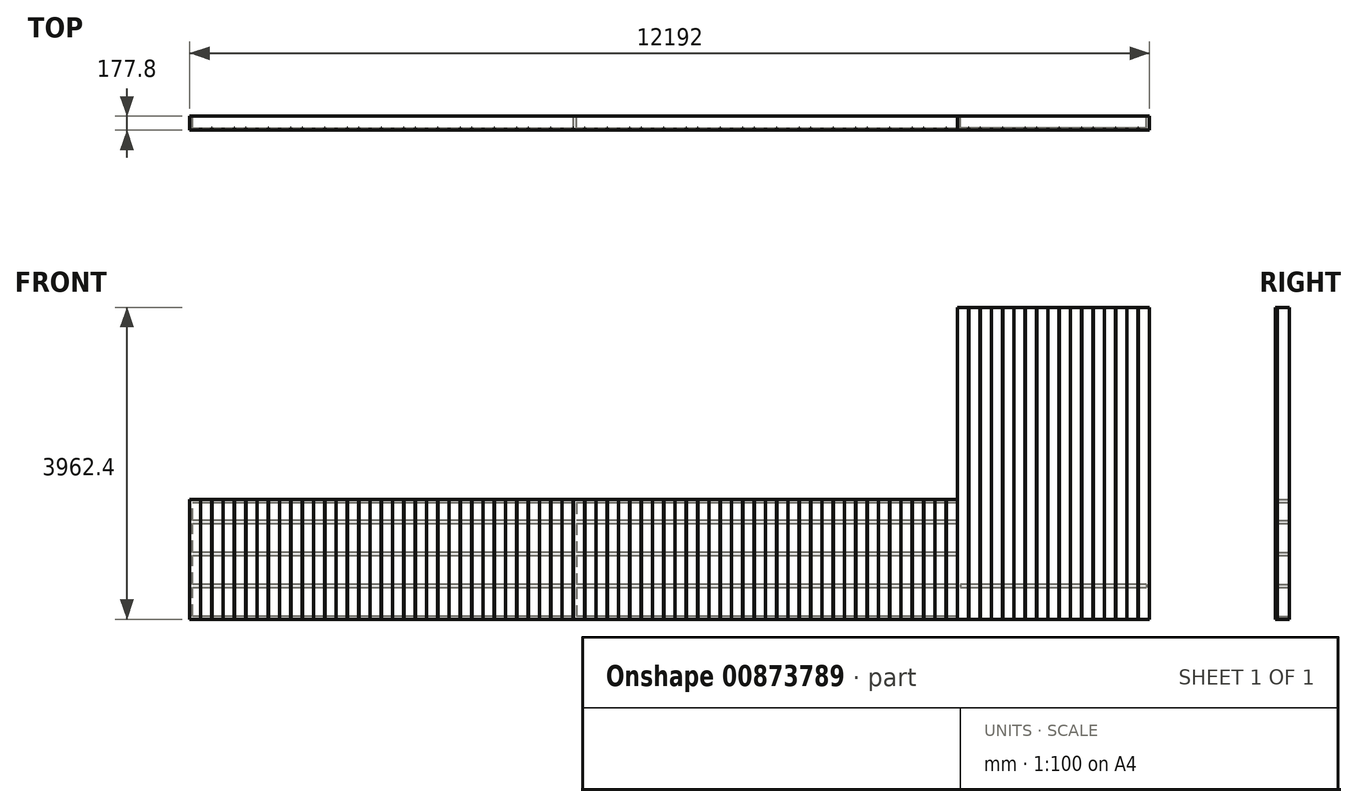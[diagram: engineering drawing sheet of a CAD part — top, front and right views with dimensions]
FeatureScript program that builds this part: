
annotation { "Feature Type Name" : "Feature", "Feature Type Description" : "" }
export const myFeature = defineFeature(function(context is Context, id is Id, definition is map)
    precondition{}
    {
        {
            var Q0;
            Q0=qCreatedBy(makeId("Front.planeOp"),FACE);
            var sketch = newSketch(context, id + "F0", { "sketchPlane" : qUnion([Q0])});
            skLineSegment(sketch, "E0", {"start": v(0, 0) * mm, "end": v(0, 1524) * mm});
            skLineSegment(sketch, "E1", {"start": v(0, 1524) * mm, "end": v(9753.6, 1524) * mm});
            skLineSegment(sketch, "E2", {"start": v(9753.6, 1524) * mm, "end": v(9753.6, 3962.4) * mm});
            skLineSegment(sketch, "E3", {"start": v(9753.6, 3962.4) * mm, "end": v(12192, 3962.4) * mm});
            skLineSegment(sketch, "E4", {"start": v(12192, 3962.4) * mm, "end": v(12192, 0) * mm});
            skLineSegment(sketch, "E5", {"start": v(12192, 0) * mm, "end": v(0, 0) * mm});
            skLineSegment(sketch, "E6.0", {"start": v(38.1, 38.1) * mm, "end": v(38.1, 1485.9) * mm});
            skLineSegment(sketch, "E6.1", {"start": v(9791.7, 1485.9) * mm, "end": v(9791.7, 3924.3) * mm});
            skLineSegment(sketch, "E6.2", {"start": v(9791.7, 3924.3) * mm, "end": v(12153.9, 3924.3) * mm});
            skLineSegment(sketch, "E6.3", {"start": v(38.1, 1485.9) * mm, "end": v(9791.7, 1485.9) * mm});
            skLineSegment(sketch, "E6.4", {"start": v(12153.9, 3924.3) * mm, "end": v(12153.9, 38.1) * mm});
            skLineSegment(sketch, "E6.5", {"start": v(12153.9, 38.1) * mm, "end": v(38.1, 38.1) * mm});
            skLineSegment(sketch, "E7", {"start": v(9791.7, 1485.9) * mm, "end": v(12153.9, 1485.9) * mm});
            skLineSegment(sketch, "E8", {"start": v(12153.9, 1524) * mm, "end": v(9791.7, 1524) * mm});
            skLineSegment(sketch, "E9", {"start": v(9791.7, 1485.9) * mm, "end": v(9791.7, 38.1) * mm});
            skLineSegment(sketch, "E10", {"start": v(9753.6, 1485.9) * mm, "end": v(9753.6, 38.1) * mm});
            skLineSegment(sketch, "E11", {"start": v(19.05, 0) * mm, "end": v(19.05, 1524) * mm, "construction": true});
            skLineSegment(sketch, "E12", {"start": v(4895.85, 1524) * mm, "end": v(4895.85, 0) * mm, "construction": true});
            skLineSegment(sketch, "E13.0", {"start": v(4876.8, 1524) * mm, "end": v(4876.8, 0) * mm});
            skLineSegment(sketch, "E14.0", {"start": v(4914.9, 1524) * mm, "end": v(4914.9, 0) * mm});
            skLineSegment(sketch, "E15", {"start": v(0, 19.05) * mm, "end": v(12192, 19.05) * mm, "construction": true});
            skLineSegment(sketch, "E16", {"start": v(38.1, 425.45) * mm, "end": v(4876.8, 425.45) * mm, "construction": true});
            skLineSegment(sketch, "E17.0.1.0", {"start": v(38.1, 831.85) * mm, "end": v(4876.8, 831.85) * mm, "construction": true});
            skLineSegment(sketch, "E17.0.2.0", {"start": v(38.1, 1238.25) * mm, "end": v(4876.8, 1238.25) * mm, "construction": true});
            skLineSegment(sketch, "E17.direction1", {"start": v(38.1, 425.45) * mm, "end": v(38.1, 425.45) * mm});
            skLineSegment(sketch, "E17.direction2", {"start": v(38.1, 425.45) * mm, "end": v(38.1, 831.85) * mm, "construction": true});
            skLineSegment(sketch, "E18", {"start": v(4914.9, 1238.25) * mm, "end": v(9753.6, 1238.25) * mm, "construction": true});
            skLineSegment(sketch, "E19", {"start": v(4914.9, 831.85) * mm, "end": v(9753.6, 831.85) * mm, "construction": true});
            skLineSegment(sketch, "E20", {"start": v(4914.9, 425.45) * mm, "end": v(9753.6, 425.45) * mm, "construction": true});
            skLineSegment(sketch, "E21", {"start": v(9791.7, 1238.25) * mm, "end": v(12153.9, 1238.25) * mm, "construction": true});
            skLineSegment(sketch, "E22", {"start": v(9791.7, 831.85) * mm, "end": v(12153.9, 831.85) * mm, "construction": true});
            skLineSegment(sketch, "E23", {"start": v(9791.7, 425.45) * mm, "end": v(12153.9, 425.45) * mm, "construction": true});
            skLineSegment(sketch, "E24", {"start": v(12153.9, 425.45) * mm, "end": v(12153.9, 1485.9) * mm});
            skLineSegment(sketch, "E25", {"start": v(12153.9, 1504.95) * mm, "end": v(9791.7, 1504.95) * mm, "construction": true});
            skLineSegment(sketch, "E26", {"start": v(9791.7, 1911.35) * mm, "end": v(12153.9, 1911.35) * mm, "construction": true});
            skLineSegment(sketch, "E27.0.1.0", {"start": v(9791.7, 2317.75) * mm, "end": v(12153.9, 2317.75) * mm, "construction": true});
            skLineSegment(sketch, "E27.0.2.0", {"start": v(9791.7, 2724.15) * mm, "end": v(12153.9, 2724.15) * mm, "construction": true});
            skLineSegment(sketch, "E27.0.3.0", {"start": v(9791.7, 3130.55) * mm, "end": v(12153.9, 3130.55) * mm, "construction": true});
            skLineSegment(sketch, "E27.0.4.0", {"start": v(9791.7, 3536.95) * mm, "end": v(12153.9, 3536.95) * mm, "construction": true});
            skLineSegment(sketch, "E27.direction1", {"start": v(9791.7, 1911.35) * mm, "end": v(9791.7, 1911.35) * mm});
            skLineSegment(sketch, "E27.direction2", {"start": v(9791.7, 1911.35) * mm, "end": v(9791.7, 2317.75) * mm, "construction": true});
            skLineSegment(sketch, "E28", {"start": v(38.1, 406.4) * mm, "end": v(12153.9, 406.4) * mm});
            skLineSegment(sketch, "E29", {"start": v(12153.9, 444.5) * mm, "end": v(38.1, 444.5) * mm});
            skLineSegment(sketch, "E30", {"start": v(38.1, 812.8) * mm, "end": v(12153.9, 812.8) * mm});
            skLineSegment(sketch, "E31", {"start": v(12153.9, 850.9) * mm, "end": v(38.1, 850.9) * mm});
            skLineSegment(sketch, "E32", {"start": v(38.1, 850.9) * mm, "end": v(70.73, 865.43) * mm});
            skLineSegment(sketch, "E33", {"start": v(38.1, 1219.2) * mm, "end": v(12153.9, 1219.2) * mm});
            skLineSegment(sketch, "E34", {"start": v(12153.9, 1257.3) * mm, "end": v(38.1, 1257.3) * mm});
            skLineSegment(sketch, "E35", {"start": v(9791.7, 1892.3) * mm, "end": v(12153.9, 1892.3) * mm});
            skLineSegment(sketch, "E36", {"start": v(9791.7, 1930.4) * mm, "end": v(12153.9, 1930.4) * mm});
            skLineSegment(sketch, "E37", {"start": v(12153.9, 2298.7) * mm, "end": v(9791.7, 2298.7) * mm});
            skLineSegment(sketch, "E38", {"start": v(9791.7, 2336.8) * mm, "end": v(12153.9, 2336.8) * mm});
            skLineSegment(sketch, "E39", {"start": v(12153.9, 2336.8) * mm, "end": v(12144.47, 2361.14) * mm});
            skLineSegment(sketch, "E40", {"start": v(12153.9, 2705.1) * mm, "end": v(9791.7, 2705.1) * mm});
            skLineSegment(sketch, "E41", {"start": v(9791.7, 2743.2) * mm, "end": v(12153.9, 2743.2) * mm});
            skLineSegment(sketch, "E42", {"start": v(12153.9, 3111.5) * mm, "end": v(9791.7, 3111.5) * mm});
            skLineSegment(sketch, "E43", {"start": v(9791.7, 3149.6) * mm, "end": v(12153.9, 3149.6) * mm});
            skLineSegment(sketch, "E44", {"start": v(12153.9, 3517.9) * mm, "end": v(9791.7, 3517.9) * mm});
            skLineSegment(sketch, "E45", {"start": v(9791.7, 3556) * mm, "end": v(12153.9, 3556) * mm});
            skSolve(sketch);
        }
        {
            var Q0;
            Q0 = qSketchRegion(id + "F0", true);
            var Q1;
            {var subQ0=sQuery(id+"F0.wireOp",EDGE,"E33");var subQ1=sQuery(id+"F0.wireOp",EDGE,"E6.0");var subQ2=makeQuery(id+"F0.imprint","INTERSECT",VERTEX,{"derivedFrom":[subQ1,subQ0]});Q1=makeQuery(id+"F0.imprint","IMPRINT",FACE,{"disambiguationData":[TD([[makeQuery(id+"F0.imprint","IMPRINT",EDGE,{"disambiguationData":[TD([[subQ2,-1.0]])],"derivedFrom":subQ1}),-1.0]])]});}
            var Q2;
            {var subQ0=sQuery(id+"F0.wireOp",EDGE,"E34");var subQ1=sQuery(id+"F0.wireOp",EDGE,"E10");var subQ2=makeQuery(id+"F0.imprint","INTERSECT",VERTEX,{"derivedFrom":[subQ1,subQ0]});Q2=makeQuery(id+"F0.imprint","IMPRINT",FACE,{"disambiguationData":[TD([[makeQuery(id+"F0.imprint","IMPRINT",EDGE,{"disambiguationData":[TD([[subQ2,-1.0]])],"derivedFrom":subQ1}),-1.0]])]});}
            var Q3;
            {var subQ0=sQuery(id+"F0.wireOp",EDGE,"E13.0");var subQ1=sQuery(id+"F0.wireOp",EDGE,"E6.3");var subQ2=makeQuery(id+"F0.imprint","INTERSECT",VERTEX,{"derivedFrom":[subQ1,subQ0]});Q3=makeQuery(id+"F0.imprint","IMPRINT",FACE,{"disambiguationData":[TD([[makeQuery(id+"F0.imprint","IMPRINT",EDGE,{"disambiguationData":[TD([[subQ2,-1.0]])],"derivedFrom":subQ1}),-1.0]])]});}
            var Q4;
            {var subQ0=sQuery(id+"F0.wireOp",EDGE,"E33");var subQ1=sQuery(id+"F0.wireOp",EDGE,"E13.0");var subQ2=makeQuery(id+"F0.imprint","INTERSECT",VERTEX,{"derivedFrom":[subQ1,subQ0]});Q4=makeQuery(id+"F0.imprint","IMPRINT",FACE,{"disambiguationData":[TD([[makeQuery(id+"F0.imprint","IMPRINT",EDGE,{"disambiguationData":[TD([[subQ2,-1.0]])],"derivedFrom":subQ1}),1.0]])]});}
            var Q5;
            {var subQ0=sQuery(id+"F0.wireOp",EDGE,"E34");var subQ1=sQuery(id+"F0.wireOp",EDGE,"E13.0");var subQ2=makeQuery(id+"F0.imprint","INTERSECT",VERTEX,{"derivedFrom":[subQ1,subQ0]});Q5=makeQuery(id+"F0.imprint","IMPRINT",FACE,{"disambiguationData":[TD([[makeQuery(id+"F0.imprint","IMPRINT",EDGE,{"disambiguationData":[TD([[subQ2,-1.0]])],"derivedFrom":subQ1}),1.0]])]});}
            var Q6;
            {var subQ0=sQuery(id+"F0.wireOp",EDGE,"E31");var subQ1=sQuery(id+"F0.wireOp",EDGE,"E13.0");var subQ2=makeQuery(id+"F0.imprint","INTERSECT",VERTEX,{"derivedFrom":[subQ1,subQ0]});Q6=makeQuery(id+"F0.imprint","IMPRINT",FACE,{"disambiguationData":[TD([[makeQuery(id+"F0.imprint","IMPRINT",EDGE,{"disambiguationData":[TD([[subQ2,-1.0]])],"derivedFrom":subQ1}),1.0]])]});}
            var Q7;
            {var subQ0=sQuery(id+"F0.wireOp",EDGE,"E31");var subQ1=sQuery(id+"F0.wireOp",EDGE,"E10");var subQ2=makeQuery(id+"F0.imprint","INTERSECT",VERTEX,{"derivedFrom":[subQ1,subQ0]});Q7=makeQuery(id+"F0.imprint","IMPRINT",FACE,{"disambiguationData":[TD([[makeQuery(id+"F0.imprint","IMPRINT",EDGE,{"disambiguationData":[TD([[subQ2,-1.0]])],"derivedFrom":subQ1}),-1.0]])]});}
            var Q8;
            {var subQ0=sQuery(id+"F0.wireOp",EDGE,"E30");var subQ1=sQuery(id+"F0.wireOp",EDGE,"E6.0");var subQ2=makeQuery(id+"F0.imprint","INTERSECT",VERTEX,{"derivedFrom":[subQ1,subQ0]});Q8=makeQuery(id+"F0.imprint","IMPRINT",FACE,{"disambiguationData":[TD([[makeQuery(id+"F0.imprint","IMPRINT",EDGE,{"disambiguationData":[TD([[subQ2,-1.0]])],"derivedFrom":subQ1}),-1.0]])]});}
            var Q9;
            {var subQ0=sQuery(id+"F0.wireOp",EDGE,"E30");var subQ1=sQuery(id+"F0.wireOp",EDGE,"E13.0");var subQ2=makeQuery(id+"F0.imprint","INTERSECT",VERTEX,{"derivedFrom":[subQ1,subQ0]});Q9=makeQuery(id+"F0.imprint","IMPRINT",FACE,{"disambiguationData":[TD([[makeQuery(id+"F0.imprint","IMPRINT",EDGE,{"disambiguationData":[TD([[subQ2,-1.0]])],"derivedFrom":subQ1}),1.0]])]});}
            var Q10;
            {var subQ0=sQuery(id+"F0.wireOp",EDGE,"E14.0");var subQ1=sQuery(id+"F0.wireOp",EDGE,"E6.5");var subQ2=makeQuery(id+"F0.imprint","INTERSECT",VERTEX,{"derivedFrom":[subQ1,subQ0]});Q10=makeQuery(id+"F0.imprint","IMPRINT",FACE,{"disambiguationData":[TD([[makeQuery(id+"F0.imprint","IMPRINT",EDGE,{"disambiguationData":[TD([[subQ2,-1.0]])],"derivedFrom":subQ1}),-1.0]])]});}
            var Q11;
            {var subQ0=sQuery(id+"F0.wireOp",EDGE,"E29");var subQ1=sQuery(id+"F0.wireOp",EDGE,"E13.0");var subQ2=makeQuery(id+"F0.imprint","INTERSECT",VERTEX,{"derivedFrom":[subQ1,subQ0]});Q11=makeQuery(id+"F0.imprint","IMPRINT",FACE,{"disambiguationData":[TD([[makeQuery(id+"F0.imprint","IMPRINT",EDGE,{"disambiguationData":[TD([[subQ2,-1.0]])],"derivedFrom":subQ1}),1.0]])]});}
            var Q12;
            {var subQ0=sQuery(id+"F0.wireOp",EDGE,"E28");var subQ1=sQuery(id+"F0.wireOp",EDGE,"E6.0");var subQ2=makeQuery(id+"F0.imprint","INTERSECT",VERTEX,{"derivedFrom":[subQ1,subQ0]});Q12=makeQuery(id+"F0.imprint","IMPRINT",FACE,{"disambiguationData":[TD([[makeQuery(id+"F0.imprint","IMPRINT",EDGE,{"disambiguationData":[TD([[subQ2,-1.0]])],"derivedFrom":subQ1}),-1.0]])]});}
            var Q13;
            {var subQ0=sQuery(id+"F0.wireOp",EDGE,"E29");var subQ1=sQuery(id+"F0.wireOp",EDGE,"E10");var subQ2=makeQuery(id+"F0.imprint","INTERSECT",VERTEX,{"derivedFrom":[subQ1,subQ0]});Q13=makeQuery(id+"F0.imprint","IMPRINT",FACE,{"disambiguationData":[TD([[makeQuery(id+"F0.imprint","IMPRINT",EDGE,{"disambiguationData":[TD([[subQ2,-1.0]])],"derivedFrom":subQ1}),-1.0]])]});}
            var Q14;
            {var subQ1=sQuery(id+"F0.wireOp",EDGE,"E6.3");var subQ3=sQuery(id+"F0.wireOp",EDGE,"E10");var subQ4=makeQuery(id+"F0.imprint","INTERSECT",VERTEX,{"derivedFrom":[subQ1,subQ3]});Q14=makeQuery(id+"F0.imprint","IMPRINT",FACE,{"disambiguationData":[TD([[makeQuery(id+"F0.imprint","IMPRINT",EDGE,{"disambiguationData":[TD([[subQ4,-1.0]])],"derivedFrom":subQ3}),1.0]])]});}
            var Q15;
            {var subQ0=sQuery(id+"F0.wireOp",EDGE,"E34");var subQ1=sQuery(id+"F0.wireOp",EDGE,"E9");var subQ2=makeQuery(id+"F0.imprint","INTERSECT",VERTEX,{"derivedFrom":[subQ1,subQ0]});Q15=makeQuery(id+"F0.imprint","IMPRINT",FACE,{"disambiguationData":[TD([[makeQuery(id+"F0.imprint","IMPRINT",EDGE,{"disambiguationData":[TD([[subQ2,-1.0]])],"derivedFrom":subQ1}),-1.0]])]});}
            var Q16;
            {var subQ0=sQuery(id+"F0.wireOp",EDGE,"E33");var subQ1=sQuery(id+"F0.wireOp",EDGE,"E9");var subQ2=makeQuery(id+"F0.imprint","INTERSECT",VERTEX,{"derivedFrom":[subQ1,subQ0]});Q16=makeQuery(id+"F0.imprint","IMPRINT",FACE,{"disambiguationData":[TD([[makeQuery(id+"F0.imprint","IMPRINT",EDGE,{"disambiguationData":[TD([[subQ2,-1.0]])],"derivedFrom":subQ1}),-1.0]])]});}
            var Q17;
            {var subQ0=sQuery(id+"F0.wireOp",EDGE,"E31");var subQ1=sQuery(id+"F0.wireOp",EDGE,"E9");var subQ2=makeQuery(id+"F0.imprint","INTERSECT",VERTEX,{"derivedFrom":[subQ1,subQ0]});Q17=makeQuery(id+"F0.imprint","IMPRINT",FACE,{"disambiguationData":[TD([[makeQuery(id+"F0.imprint","IMPRINT",EDGE,{"disambiguationData":[TD([[subQ2,-1.0]])],"derivedFrom":subQ1}),-1.0]])]});}
            var Q18;
            {var subQ0=sQuery(id+"F0.wireOp",EDGE,"E30");var subQ1=sQuery(id+"F0.wireOp",EDGE,"E9");var subQ2=makeQuery(id+"F0.imprint","INTERSECT",VERTEX,{"derivedFrom":[subQ1,subQ0]});Q18=makeQuery(id+"F0.imprint","IMPRINT",FACE,{"disambiguationData":[TD([[makeQuery(id+"F0.imprint","IMPRINT",EDGE,{"disambiguationData":[TD([[subQ2,-1.0]])],"derivedFrom":subQ1}),-1.0]])]});}
            var Q19;
            {var subQ0=sQuery(id+"F0.wireOp",EDGE,"E29");var subQ1=sQuery(id+"F0.wireOp",EDGE,"E9");var subQ2=makeQuery(id+"F0.imprint","INTERSECT",VERTEX,{"derivedFrom":[subQ1,subQ0]});Q19=makeQuery(id+"F0.imprint","IMPRINT",FACE,{"disambiguationData":[TD([[makeQuery(id+"F0.imprint","IMPRINT",EDGE,{"disambiguationData":[TD([[subQ2,-1.0]])],"derivedFrom":subQ1}),-1.0]])]});}
            var Q20;
            {var subQ0=sQuery(id+"F0.wireOp",EDGE,"E9");var subQ1=sQuery(id+"F0.wireOp",EDGE,"E6.5");var subQ2=makeQuery(id+"F0.imprint","INTERSECT",VERTEX,{"derivedFrom":[subQ1,subQ0]});Q20=makeQuery(id+"F0.imprint","IMPRINT",FACE,{"disambiguationData":[TD([[makeQuery(id+"F0.imprint","IMPRINT",EDGE,{"disambiguationData":[TD([[subQ2,-1.0]])],"derivedFrom":subQ1}),-1.0]])]});}
            var Q21;
            {var subQ1=sQuery(id+"F0.wireOp",EDGE,"E6.4");var subQ5=sQuery(id+"F0.wireOp",EDGE,"E24");var subQ6=makeQuery(id+"F0.imprint","INTERSECT",VERTEX,{"derivedFrom":[subQ1,subQ5]});Q21=makeQuery(id+"F0.imprint","IMPRINT",FACE,{"disambiguationData":[TD([[makeQuery(id+"F0.imprint","IMPRINT",EDGE,{"disambiguationData":[TD([[subQ6,-1.0]])],"derivedFrom":subQ1}),-1.0]])]});}
            var Q22;
            {var subQ0=sQuery(id+"F0.wireOp",EDGE,"E31");var subQ1=sQuery(id+"F0.wireOp",EDGE,"E9");var subQ2=makeQuery(id+"F0.imprint","INTERSECT",VERTEX,{"derivedFrom":[subQ1,subQ0]});Q22=makeQuery(id+"F0.imprint","IMPRINT",FACE,{"disambiguationData":[TD([[makeQuery(id+"F0.imprint","IMPRINT",EDGE,{"disambiguationData":[TD([[subQ2,-1.0]])],"derivedFrom":subQ1}),1.0]])]});}
            var Q23;
            {var subQ0=sQuery(id+"F0.wireOp",EDGE,"E34");var subQ1=sQuery(id+"F0.wireOp",EDGE,"E9");var subQ2=makeQuery(id+"F0.imprint","INTERSECT",VERTEX,{"derivedFrom":[subQ1,subQ0]});Q23=makeQuery(id+"F0.imprint","IMPRINT",FACE,{"disambiguationData":[TD([[makeQuery(id+"F0.imprint","IMPRINT",EDGE,{"disambiguationData":[TD([[subQ2,-1.0]])],"derivedFrom":subQ1}),1.0]])]});}
            var Q24;
            {var subQ0=sQuery(id+"F0.wireOp",EDGE,"E7");Q24=makeQuery(id+"F0.imprint","IMPRINT",FACE,{"disambiguationData":[TD([[makeQuery(id+"F0.imprint","IMPRINT",EDGE,{"derivedFrom":subQ0}),1.0]])]});}
            var Q25;
            {var subQ0=sQuery(id+"F0.wireOp",EDGE,"E35");Q25=makeQuery(id+"F0.imprint","IMPRINT",FACE,{"disambiguationData":[TD([[makeQuery(id+"F0.imprint","IMPRINT",EDGE,{"derivedFrom":subQ0}),1.0]])]});}
            var Q26;
            {var subQ0=sQuery(id+"F0.wireOp",EDGE,"E37");Q26=makeQuery(id+"F0.imprint","IMPRINT",FACE,{"disambiguationData":[TD([[makeQuery(id+"F0.imprint","IMPRINT",EDGE,{"derivedFrom":subQ0}),-1.0]])]});}
            var Q27;
            {var subQ0=sQuery(id+"F0.wireOp",EDGE,"E42");Q27=makeQuery(id+"F0.imprint","IMPRINT",FACE,{"disambiguationData":[TD([[makeQuery(id+"F0.imprint","IMPRINT",EDGE,{"derivedFrom":subQ0}),-1.0]])]});}
            var Q28;
            {var subQ0=sQuery(id+"F0.wireOp",EDGE,"E44");Q28=makeQuery(id+"F0.imprint","IMPRINT",FACE,{"disambiguationData":[TD([[makeQuery(id+"F0.imprint","IMPRINT",EDGE,{"derivedFrom":subQ0}),-1.0]])]});}
            var Q29;
            {var subQ0=sQuery(id+"F0.wireOp",EDGE,"E40");Q29=makeQuery(id+"F0.imprint","IMPRINT",FACE,{"disambiguationData":[TD([[makeQuery(id+"F0.imprint","IMPRINT",EDGE,{"derivedFrom":subQ0}),-1.0]])]});}
            extrude(context, id + "F1", {"entities" : qUnion([Q0, Q1, Q2, Q3, Q4, Q5, Q6, Q7, Q8, Q9, Q10, Q11, Q12, Q13, Q14, Q15, Q16, Q17, Q18, Q19, Q20, Q21, Q22, Q23, Q24, Q25, Q26, Q27, Q28, Q29]), "depth" : 152.4 * mm, "offsetDistance" : 25.4 * mm});
        }
        {
            var Q0;
            Q0=makeQuery(id+"F1.opExtrude","CAP_FACE",FACE,{"disambiguationData":[OSD([sQuery(id+"F0.wireOp",EDGE,"E0"),sQuery(id+"F0.wireOp",EDGE,"E1"),sQuery(id+"F0.wireOp",EDGE,"E2"),sQuery(id+"F0.wireOp",EDGE,"E3"),sQuery(id+"F0.wireOp",EDGE,"E4"),sQuery(id+"F0.wireOp",EDGE,"E5"),sQuery(id+"F0.wireOp",EDGE,"E6.0"),sQuery(id+"F0.wireOp",EDGE,"E6.1"),sQuery(id+"F0.wireOp",EDGE,"E6.2"),sQuery(id+"F0.wireOp",EDGE,"E6.3"),sQuery(id+"F0.wireOp",EDGE,"E6.4"),sQuery(id+"F0.wireOp",EDGE,"E6.5"),sQuery(id+"F0.wireOp",EDGE,"E7"),sQuery(id+"F0.wireOp",EDGE,"E8"),sQuery(id+"F0.wireOp",EDGE,"E9"),sQuery(id+"F0.wireOp",EDGE,"E10"),sQuery(id+"F0.wireOp",EDGE,"E13.0"),sQuery(id+"F0.wireOp",EDGE,"E14.0"),sQuery(id+"F0.wireOp",EDGE,"E24"),sQuery(id+"F0.wireOp",EDGE,"E28"),sQuery(id+"F0.wireOp",EDGE,"E29"),sQuery(id+"F0.wireOp",EDGE,"E30"),sQuery(id+"F0.wireOp",EDGE,"E31"),sQuery(id+"F0.wireOp",EDGE,"E33"),sQuery(id+"F0.wireOp",EDGE,"E34"),sQuery(id+"F0.wireOp",EDGE,"E35"),sQuery(id+"F0.wireOp",EDGE,"E36"),sQuery(id+"F0.wireOp",EDGE,"E37"),sQuery(id+"F0.wireOp",EDGE,"E38"),sQuery(id+"F0.wireOp",EDGE,"E40"),sQuery(id+"F0.wireOp",EDGE,"E41"),sQuery(id+"F0.wireOp",EDGE,"E42"),sQuery(id+"F0.wireOp",EDGE,"E43"),sQuery(id+"F0.wireOp",EDGE,"E44"),sQuery(id+"F0.wireOp",EDGE,"E45")])],"isStart":false});
            var sketch = newSketch(context, id + "F2", { "sketchPlane" : qUnion([Q0])});
            skLineSegment(sketch, "E46.bottom", {"start": v(9753.6, 3962.4) * mm, "end": v(9893.3, 3962.4) * mm});
            skLineSegment(sketch, "E46.top", {"start": v(9753.6, 0) * mm, "end": v(9893.3, 0) * mm});
            skLineSegment(sketch, "E46.left", {"start": v(9753.6, 3962.4) * mm, "end": v(9753.6, 0) * mm});
            skLineSegment(sketch, "E46.right", {"start": v(9893.3, 3962.4) * mm, "end": v(9893.3, 0) * mm});
            skLineSegment(sketch, "E47.1.0.0", {"start": v(10036.81, 3962.4) * mm, "end": v(10036.81, 0) * mm});
            skLineSegment(sketch, "E47.1.0.1", {"start": v(9897.1, 3962.4) * mm, "end": v(10036.81, 3962.4) * mm});
            skLineSegment(sketch, "E47.1.0.2", {"start": v(9897.1, 3962.4) * mm, "end": v(9897.1, 0) * mm});
            skLineSegment(sketch, "E47.1.0.3", {"start": v(9897.1, 0) * mm, "end": v(10036.81, 0) * mm});
            skLineSegment(sketch, "E47.2.0.0", {"start": v(10180.32, 3962.4) * mm, "end": v(10180.32, 0) * mm});
            skLineSegment(sketch, "E47.2.0.1", {"start": v(10040.62, 3962.4) * mm, "end": v(10180.32, 3962.4) * mm});
            skLineSegment(sketch, "E47.2.0.2", {"start": v(10040.62, 3962.4) * mm, "end": v(10040.62, 0) * mm});
            skLineSegment(sketch, "E47.2.0.3", {"start": v(10040.62, 0) * mm, "end": v(10180.32, 0) * mm});
            skLineSegment(sketch, "E47.3.0.0", {"start": v(10323.83, 3962.4) * mm, "end": v(10323.83, 0) * mm});
            skLineSegment(sketch, "E47.3.0.1", {"start": v(10184.13, 3962.4) * mm, "end": v(10323.83, 3962.4) * mm});
            skLineSegment(sketch, "E47.3.0.2", {"start": v(10184.13, 3962.4) * mm, "end": v(10184.13, 0) * mm});
            skLineSegment(sketch, "E47.3.0.3", {"start": v(10184.13, 0) * mm, "end": v(10323.83, 0) * mm});
            skLineSegment(sketch, "E47.4.0.0", {"start": v(10467.34, 3962.4) * mm, "end": v(10467.34, 0) * mm});
            skLineSegment(sketch, "E47.4.0.1", {"start": v(10327.64, 3962.4) * mm, "end": v(10467.34, 3962.4) * mm});
            skLineSegment(sketch, "E47.4.0.2", {"start": v(10327.64, 3962.4) * mm, "end": v(10327.64, 0) * mm});
            skLineSegment(sketch, "E47.4.0.3", {"start": v(10327.64, 0) * mm, "end": v(10467.34, 0) * mm});
            skLineSegment(sketch, "E47.5.0.0", {"start": v(10610.85, 3962.4) * mm, "end": v(10610.85, 0) * mm});
            skLineSegment(sketch, "E47.5.0.1", {"start": v(10471.15, 3962.4) * mm, "end": v(10610.85, 3962.4) * mm});
            skLineSegment(sketch, "E47.5.0.2", {"start": v(10471.15, 3962.4) * mm, "end": v(10471.15, 0) * mm});
            skLineSegment(sketch, "E47.5.0.3", {"start": v(10471.15, 0) * mm, "end": v(10610.85, 0) * mm});
            skLineSegment(sketch, "E47.6.0.0", {"start": v(10754.36, 3962.4) * mm, "end": v(10754.36, 0) * mm});
            skLineSegment(sketch, "E47.6.0.1", {"start": v(10614.66, 3962.4) * mm, "end": v(10754.36, 3962.4) * mm});
            skLineSegment(sketch, "E47.6.0.2", {"start": v(10614.66, 3962.4) * mm, "end": v(10614.66, 0) * mm});
            skLineSegment(sketch, "E47.6.0.3", {"start": v(10614.66, 0) * mm, "end": v(10754.36, 0) * mm});
            skLineSegment(sketch, "E47.7.0.0", {"start": v(10897.87, 3962.4) * mm, "end": v(10897.87, 0) * mm});
            skLineSegment(sketch, "E47.7.0.1", {"start": v(10758.17, 3962.4) * mm, "end": v(10897.87, 3962.4) * mm});
            skLineSegment(sketch, "E47.7.0.2", {"start": v(10758.17, 3962.4) * mm, "end": v(10758.17, 0) * mm});
            skLineSegment(sketch, "E47.7.0.3", {"start": v(10758.17, 0) * mm, "end": v(10897.87, 0) * mm});
            skLineSegment(sketch, "E47.8.0.0", {"start": v(11041.38, 3962.4) * mm, "end": v(11041.38, 0) * mm});
            skLineSegment(sketch, "E47.8.0.1", {"start": v(10901.68, 3962.4) * mm, "end": v(11041.38, 3962.4) * mm});
            skLineSegment(sketch, "E47.8.0.2", {"start": v(10901.68, 3962.4) * mm, "end": v(10901.68, 0) * mm});
            skLineSegment(sketch, "E47.8.0.3", {"start": v(10901.68, 0) * mm, "end": v(11041.38, 0) * mm});
            skLineSegment(sketch, "E47.9.0.0", {"start": v(11184.89, 3962.4) * mm, "end": v(11184.89, 0) * mm});
            skLineSegment(sketch, "E47.9.0.1", {"start": v(11045.19, 3962.4) * mm, "end": v(11184.89, 3962.4) * mm});
            skLineSegment(sketch, "E47.9.0.2", {"start": v(11045.19, 3962.4) * mm, "end": v(11045.19, 0) * mm});
            skLineSegment(sketch, "E47.9.0.3", {"start": v(11045.19, 0) * mm, "end": v(11184.89, 0) * mm});
            skLineSegment(sketch, "E47.10.0.0", {"start": v(11328.4, 3962.4) * mm, "end": v(11328.4, 0) * mm});
            skLineSegment(sketch, "E47.10.0.1", {"start": v(11188.7, 3962.4) * mm, "end": v(11328.4, 3962.4) * mm});
            skLineSegment(sketch, "E47.10.0.2", {"start": v(11188.7, 3962.4) * mm, "end": v(11188.7, 0) * mm});
            skLineSegment(sketch, "E47.10.0.3", {"start": v(11188.7, 0) * mm, "end": v(11328.4, 0) * mm});
            skLineSegment(sketch, "E47.11.0.0", {"start": v(11471.9, 3962.4) * mm, "end": v(11471.9, 0) * mm});
            skLineSegment(sketch, "E47.11.0.1", {"start": v(11332.2, 3962.4) * mm, "end": v(11471.9, 3962.4) * mm});
            skLineSegment(sketch, "E47.11.0.2", {"start": v(11332.2, 3962.4) * mm, "end": v(11332.2, 0) * mm});
            skLineSegment(sketch, "E47.11.0.3", {"start": v(11332.2, 0) * mm, "end": v(11471.9, 0) * mm});
            skLineSegment(sketch, "E47.12.0.0", {"start": v(11615.42, 3962.4) * mm, "end": v(11615.42, 0) * mm});
            skLineSegment(sketch, "E47.12.0.1", {"start": v(11475.72, 3962.4) * mm, "end": v(11615.42, 3962.4) * mm});
            skLineSegment(sketch, "E47.12.0.2", {"start": v(11475.72, 3962.4) * mm, "end": v(11475.72, 0) * mm});
            skLineSegment(sketch, "E47.12.0.3", {"start": v(11475.72, 0) * mm, "end": v(11615.42, 0) * mm});
            skLineSegment(sketch, "E47.13.0.0", {"start": v(11758.93, 3962.4) * mm, "end": v(11758.93, 0) * mm});
            skLineSegment(sketch, "E47.13.0.1", {"start": v(11619.23, 3962.4) * mm, "end": v(11758.93, 3962.4) * mm});
            skLineSegment(sketch, "E47.13.0.2", {"start": v(11619.23, 3962.4) * mm, "end": v(11619.23, 0) * mm});
            skLineSegment(sketch, "E47.13.0.3", {"start": v(11619.23, 0) * mm, "end": v(11758.93, 0) * mm});
            skLineSegment(sketch, "E47.14.0.0", {"start": v(11902.44, 3962.4) * mm, "end": v(11902.44, 0) * mm});
            skLineSegment(sketch, "E47.14.0.1", {"start": v(11762.74, 3962.4) * mm, "end": v(11902.44, 3962.4) * mm});
            skLineSegment(sketch, "E47.14.0.2", {"start": v(11762.74, 3962.4) * mm, "end": v(11762.74, 0) * mm});
            skLineSegment(sketch, "E47.14.0.3", {"start": v(11762.74, 0) * mm, "end": v(11902.44, 0) * mm});
            skLineSegment(sketch, "E47.15.0.0", {"start": v(12045.95, 3962.4) * mm, "end": v(12045.95, 0) * mm});
            skLineSegment(sketch, "E47.15.0.1", {"start": v(11906.25, 3962.4) * mm, "end": v(12045.95, 3962.4) * mm});
            skLineSegment(sketch, "E47.15.0.2", {"start": v(11906.25, 3962.4) * mm, "end": v(11906.25, 0) * mm});
            skLineSegment(sketch, "E47.15.0.3", {"start": v(11906.25, 0) * mm, "end": v(12045.95, 0) * mm});
            skLineSegment(sketch, "E47.16.0.0", {"start": v(12189.46, 3962.4) * mm, "end": v(12189.46, 0) * mm});
            skLineSegment(sketch, "E47.16.0.1", {"start": v(12049.76, 3962.4) * mm, "end": v(12189.46, 3962.4) * mm});
            skLineSegment(sketch, "E47.16.0.2", {"start": v(12049.76, 3962.4) * mm, "end": v(12049.76, 0) * mm});
            skLineSegment(sketch, "E47.16.0.3", {"start": v(12049.76, 0) * mm, "end": v(12189.46, 0) * mm});
            skLineSegment(sketch, "E47.direction1", {"start": v(9893.3, 0) * mm, "end": v(10036.81, 0) * mm, "construction": true});
            skLineSegment(sketch, "E48.bottom", {"start": v(9749.8, 0) * mm, "end": v(9610.1, 0) * mm});
            skLineSegment(sketch, "E48.top", {"start": v(9749.8, 1524) * mm, "end": v(9610.1, 1524) * mm});
            skLineSegment(sketch, "E48.left", {"start": v(9749.8, 0) * mm, "end": v(9749.8, 1524) * mm});
            skLineSegment(sketch, "E48.right", {"start": v(9610.1, 0) * mm, "end": v(9610.1, 1524) * mm});
            skLineSegment(sketch, "E49.1.0.0", {"start": v(9606.28, 1524) * mm, "end": v(9466.58, 1524) * mm});
            skLineSegment(sketch, "E49.1.0.1", {"start": v(9466.58, 0) * mm, "end": v(9466.58, 1524) * mm});
            skLineSegment(sketch, "E49.1.0.2", {"start": v(9606.28, 0) * mm, "end": v(9606.28, 1524) * mm});
            skLineSegment(sketch, "E49.1.0.3", {"start": v(9606.28, 0) * mm, "end": v(9466.58, 0) * mm});
            skLineSegment(sketch, "E49.2.0.0", {"start": v(9462.77, 1524) * mm, "end": v(9323.07, 1524) * mm});
            skLineSegment(sketch, "E49.2.0.1", {"start": v(9323.07, 0) * mm, "end": v(9323.07, 1524) * mm});
            skLineSegment(sketch, "E49.2.0.2", {"start": v(9462.77, 0) * mm, "end": v(9462.77, 1524) * mm});
            skLineSegment(sketch, "E49.2.0.3", {"start": v(9462.77, 0) * mm, "end": v(9323.07, 0) * mm});
            skLineSegment(sketch, "E49.3.0.0", {"start": v(9319.26, 1524) * mm, "end": v(9179.56, 1524) * mm});
            skLineSegment(sketch, "E49.3.0.1", {"start": v(9179.56, 0) * mm, "end": v(9179.56, 1524) * mm});
            skLineSegment(sketch, "E49.3.0.2", {"start": v(9319.26, 0) * mm, "end": v(9319.26, 1524) * mm});
            skLineSegment(sketch, "E49.3.0.3", {"start": v(9319.26, 0) * mm, "end": v(9179.56, 0) * mm});
            skLineSegment(sketch, "E49.4.0.0", {"start": v(9175.75, 1524) * mm, "end": v(9036.05, 1524) * mm});
            skLineSegment(sketch, "E49.4.0.1", {"start": v(9036.05, 0) * mm, "end": v(9036.05, 1524) * mm});
            skLineSegment(sketch, "E49.4.0.2", {"start": v(9175.75, 0) * mm, "end": v(9175.75, 1524) * mm});
            skLineSegment(sketch, "E49.4.0.3", {"start": v(9175.75, 0) * mm, "end": v(9036.05, 0) * mm});
            skLineSegment(sketch, "E49.5.0.0", {"start": v(9032.24, 1524) * mm, "end": v(8892.54, 1524) * mm});
            skLineSegment(sketch, "E49.5.0.1", {"start": v(8892.54, 0) * mm, "end": v(8892.54, 1524) * mm});
            skLineSegment(sketch, "E49.5.0.2", {"start": v(9032.24, 0) * mm, "end": v(9032.24, 1524) * mm});
            skLineSegment(sketch, "E49.5.0.3", {"start": v(9032.24, 0) * mm, "end": v(8892.54, 0) * mm});
            skLineSegment(sketch, "E49.6.0.0", {"start": v(8888.73, 1524) * mm, "end": v(8749.03, 1524) * mm});
            skLineSegment(sketch, "E49.6.0.1", {"start": v(8749.03, 0) * mm, "end": v(8749.03, 1524) * mm});
            skLineSegment(sketch, "E49.6.0.2", {"start": v(8888.73, 0) * mm, "end": v(8888.73, 1524) * mm});
            skLineSegment(sketch, "E49.6.0.3", {"start": v(8888.73, 0) * mm, "end": v(8749.03, 0) * mm});
            skLineSegment(sketch, "E49.7.0.0", {"start": v(8745.22, 1524) * mm, "end": v(8605.52, 1524) * mm});
            skLineSegment(sketch, "E49.7.0.1", {"start": v(8605.52, 0) * mm, "end": v(8605.52, 1524) * mm});
            skLineSegment(sketch, "E49.7.0.2", {"start": v(8745.22, 0) * mm, "end": v(8745.22, 1524) * mm});
            skLineSegment(sketch, "E49.7.0.3", {"start": v(8745.22, 0) * mm, "end": v(8605.52, 0) * mm});
            skLineSegment(sketch, "E49.8.0.0", {"start": v(8601.71, 1524) * mm, "end": v(8462.01, 1524) * mm});
            skLineSegment(sketch, "E49.8.0.1", {"start": v(8462.01, 0) * mm, "end": v(8462.01, 1524) * mm});
            skLineSegment(sketch, "E49.8.0.2", {"start": v(8601.71, 0) * mm, "end": v(8601.71, 1524) * mm});
            skLineSegment(sketch, "E49.8.0.3", {"start": v(8601.71, 0) * mm, "end": v(8462.01, 0) * mm});
            skLineSegment(sketch, "E49.9.0.0", {"start": v(8458.2, 1524) * mm, "end": v(8318.5, 1524) * mm});
            skLineSegment(sketch, "E49.9.0.1", {"start": v(8318.5, 0) * mm, "end": v(8318.5, 1524) * mm});
            skLineSegment(sketch, "E49.9.0.2", {"start": v(8458.2, 0) * mm, "end": v(8458.2, 1524) * mm});
            skLineSegment(sketch, "E49.9.0.3", {"start": v(8458.2, 0) * mm, "end": v(8318.5, 0) * mm});
            skLineSegment(sketch, "E49.10.0.0", {"start": v(8314.7, 1524) * mm, "end": v(8175, 1524) * mm});
            skLineSegment(sketch, "E49.10.0.1", {"start": v(8175, 0) * mm, "end": v(8175, 1524) * mm});
            skLineSegment(sketch, "E49.10.0.2", {"start": v(8314.7, 0) * mm, "end": v(8314.7, 1524) * mm});
            skLineSegment(sketch, "E49.10.0.3", {"start": v(8314.7, 0) * mm, "end": v(8175, 0) * mm});
            skLineSegment(sketch, "E49.11.0.0", {"start": v(8171.18, 1524) * mm, "end": v(8031.48, 1524) * mm});
            skLineSegment(sketch, "E49.11.0.1", {"start": v(8031.48, 0) * mm, "end": v(8031.48, 1524) * mm});
            skLineSegment(sketch, "E49.11.0.2", {"start": v(8171.18, 0) * mm, "end": v(8171.18, 1524) * mm});
            skLineSegment(sketch, "E49.11.0.3", {"start": v(8171.18, 0) * mm, "end": v(8031.48, 0) * mm});
            skLineSegment(sketch, "E49.12.0.0", {"start": v(8027.67, 1524) * mm, "end": v(7887.97, 1524) * mm});
            skLineSegment(sketch, "E49.12.0.1", {"start": v(7887.97, 0) * mm, "end": v(7887.97, 1524) * mm});
            skLineSegment(sketch, "E49.12.0.2", {"start": v(8027.67, 0) * mm, "end": v(8027.67, 1524) * mm});
            skLineSegment(sketch, "E49.12.0.3", {"start": v(8027.67, 0) * mm, "end": v(7887.97, 0) * mm});
            skLineSegment(sketch, "E49.13.0.0", {"start": v(7884.16, 1524) * mm, "end": v(7744.46, 1524) * mm});
            skLineSegment(sketch, "E49.13.0.1", {"start": v(7744.46, 0) * mm, "end": v(7744.46, 1524) * mm});
            skLineSegment(sketch, "E49.13.0.2", {"start": v(7884.16, 0) * mm, "end": v(7884.16, 1524) * mm});
            skLineSegment(sketch, "E49.13.0.3", {"start": v(7884.16, 0) * mm, "end": v(7744.46, 0) * mm});
            skLineSegment(sketch, "E49.14.0.0", {"start": v(7740.65, 1524) * mm, "end": v(7600.95, 1524) * mm});
            skLineSegment(sketch, "E49.14.0.1", {"start": v(7600.95, 0) * mm, "end": v(7600.95, 1524) * mm});
            skLineSegment(sketch, "E49.14.0.2", {"start": v(7740.65, 0) * mm, "end": v(7740.65, 1524) * mm});
            skLineSegment(sketch, "E49.14.0.3", {"start": v(7740.65, 0) * mm, "end": v(7600.95, 0) * mm});
            skLineSegment(sketch, "E49.15.0.0", {"start": v(7597.14, 1524) * mm, "end": v(7457.44, 1524) * mm});
            skLineSegment(sketch, "E49.15.0.1", {"start": v(7457.44, 0) * mm, "end": v(7457.44, 1524) * mm});
            skLineSegment(sketch, "E49.15.0.2", {"start": v(7597.14, 0) * mm, "end": v(7597.14, 1524) * mm});
            skLineSegment(sketch, "E49.15.0.3", {"start": v(7597.14, 0) * mm, "end": v(7457.44, 0) * mm});
            skLineSegment(sketch, "E49.16.0.0", {"start": v(7453.63, 1524) * mm, "end": v(7313.93, 1524) * mm});
            skLineSegment(sketch, "E49.16.0.1", {"start": v(7313.93, 0) * mm, "end": v(7313.93, 1524) * mm});
            skLineSegment(sketch, "E49.16.0.2", {"start": v(7453.63, 0) * mm, "end": v(7453.63, 1524) * mm});
            skLineSegment(sketch, "E49.16.0.3", {"start": v(7453.63, 0) * mm, "end": v(7313.93, 0) * mm});
            skLineSegment(sketch, "E49.17.0.0", {"start": v(7310.12, 1524) * mm, "end": v(7170.42, 1524) * mm});
            skLineSegment(sketch, "E49.17.0.1", {"start": v(7170.42, 0) * mm, "end": v(7170.42, 1524) * mm});
            skLineSegment(sketch, "E49.17.0.2", {"start": v(7310.12, 0) * mm, "end": v(7310.12, 1524) * mm});
            skLineSegment(sketch, "E49.17.0.3", {"start": v(7310.12, 0) * mm, "end": v(7170.42, 0) * mm});
            skLineSegment(sketch, "E49.18.0.0", {"start": v(7166.61, 1524) * mm, "end": v(7026.91, 1524) * mm});
            skLineSegment(sketch, "E49.18.0.1", {"start": v(7026.91, 0) * mm, "end": v(7026.91, 1524) * mm});
            skLineSegment(sketch, "E49.18.0.2", {"start": v(7166.61, 0) * mm, "end": v(7166.61, 1524) * mm});
            skLineSegment(sketch, "E49.18.0.3", {"start": v(7166.61, 0) * mm, "end": v(7026.91, 0) * mm});
            skLineSegment(sketch, "E49.19.0.0", {"start": v(7023.1, 1524) * mm, "end": v(6883.4, 1524) * mm});
            skLineSegment(sketch, "E49.19.0.1", {"start": v(6883.4, 0) * mm, "end": v(6883.4, 1524) * mm});
            skLineSegment(sketch, "E49.19.0.2", {"start": v(7023.1, 0) * mm, "end": v(7023.1, 1524) * mm});
            skLineSegment(sketch, "E49.19.0.3", {"start": v(7023.1, 0) * mm, "end": v(6883.4, 0) * mm});
            skLineSegment(sketch, "E49.20.0.0", {"start": v(6879.6, 1524) * mm, "end": v(6739.9, 1524) * mm});
            skLineSegment(sketch, "E49.20.0.1", {"start": v(6739.9, 0) * mm, "end": v(6739.9, 1524) * mm});
            skLineSegment(sketch, "E49.20.0.2", {"start": v(6879.6, 0) * mm, "end": v(6879.6, 1524) * mm});
            skLineSegment(sketch, "E49.20.0.3", {"start": v(6879.6, 0) * mm, "end": v(6739.9, 0) * mm});
            skLineSegment(sketch, "E49.21.0.0", {"start": v(6736.08, 1524) * mm, "end": v(6596.38, 1524) * mm});
            skLineSegment(sketch, "E49.21.0.1", {"start": v(6596.38, 0) * mm, "end": v(6596.38, 1524) * mm});
            skLineSegment(sketch, "E49.21.0.2", {"start": v(6736.08, 0) * mm, "end": v(6736.08, 1524) * mm});
            skLineSegment(sketch, "E49.21.0.3", {"start": v(6736.08, 0) * mm, "end": v(6596.38, 0) * mm});
            skLineSegment(sketch, "E49.22.0.0", {"start": v(6592.57, 1524) * mm, "end": v(6452.87, 1524) * mm});
            skLineSegment(sketch, "E49.22.0.1", {"start": v(6452.87, 0) * mm, "end": v(6452.87, 1524) * mm});
            skLineSegment(sketch, "E49.22.0.2", {"start": v(6592.57, 0) * mm, "end": v(6592.57, 1524) * mm});
            skLineSegment(sketch, "E49.22.0.3", {"start": v(6592.57, 0) * mm, "end": v(6452.87, 0) * mm});
            skLineSegment(sketch, "E49.23.0.0", {"start": v(6449.06, 1524) * mm, "end": v(6309.36, 1524) * mm});
            skLineSegment(sketch, "E49.23.0.1", {"start": v(6309.36, 0) * mm, "end": v(6309.36, 1524) * mm});
            skLineSegment(sketch, "E49.23.0.2", {"start": v(6449.06, 0) * mm, "end": v(6449.06, 1524) * mm});
            skLineSegment(sketch, "E49.23.0.3", {"start": v(6449.06, 0) * mm, "end": v(6309.36, 0) * mm});
            skLineSegment(sketch, "E49.24.0.0", {"start": v(6305.55, 1524) * mm, "end": v(6165.85, 1524) * mm});
            skLineSegment(sketch, "E49.24.0.1", {"start": v(6165.85, 0) * mm, "end": v(6165.85, 1524) * mm});
            skLineSegment(sketch, "E49.24.0.2", {"start": v(6305.55, 0) * mm, "end": v(6305.55, 1524) * mm});
            skLineSegment(sketch, "E49.24.0.3", {"start": v(6305.55, 0) * mm, "end": v(6165.85, 0) * mm});
            skLineSegment(sketch, "E49.25.0.0", {"start": v(6162.04, 1524) * mm, "end": v(6022.34, 1524) * mm});
            skLineSegment(sketch, "E49.25.0.1", {"start": v(6022.34, 0) * mm, "end": v(6022.34, 1524) * mm});
            skLineSegment(sketch, "E49.25.0.2", {"start": v(6162.04, 0) * mm, "end": v(6162.04, 1524) * mm});
            skLineSegment(sketch, "E49.25.0.3", {"start": v(6162.04, 0) * mm, "end": v(6022.34, 0) * mm});
            skLineSegment(sketch, "E49.26.0.0", {"start": v(6018.53, 1524) * mm, "end": v(5878.83, 1524) * mm});
            skLineSegment(sketch, "E49.26.0.1", {"start": v(5878.83, 0) * mm, "end": v(5878.83, 1524) * mm});
            skLineSegment(sketch, "E49.26.0.2", {"start": v(6018.53, 0) * mm, "end": v(6018.53, 1524) * mm});
            skLineSegment(sketch, "E49.26.0.3", {"start": v(6018.53, 0) * mm, "end": v(5878.83, 0) * mm});
            skLineSegment(sketch, "E49.27.0.0", {"start": v(5875.02, 1524) * mm, "end": v(5735.32, 1524) * mm});
            skLineSegment(sketch, "E49.27.0.1", {"start": v(5735.32, 0) * mm, "end": v(5735.32, 1524) * mm});
            skLineSegment(sketch, "E49.27.0.2", {"start": v(5875.02, 0) * mm, "end": v(5875.02, 1524) * mm});
            skLineSegment(sketch, "E49.27.0.3", {"start": v(5875.02, 0) * mm, "end": v(5735.32, 0) * mm});
            skLineSegment(sketch, "E49.28.0.0", {"start": v(5731.51, 1524) * mm, "end": v(5591.81, 1524) * mm});
            skLineSegment(sketch, "E49.28.0.1", {"start": v(5591.81, 0) * mm, "end": v(5591.81, 1524) * mm});
            skLineSegment(sketch, "E49.28.0.2", {"start": v(5731.51, 0) * mm, "end": v(5731.51, 1524) * mm});
            skLineSegment(sketch, "E49.28.0.3", {"start": v(5731.51, 0) * mm, "end": v(5591.81, 0) * mm});
            skLineSegment(sketch, "E49.29.0.0", {"start": v(5588, 1524) * mm, "end": v(5448.3, 1524) * mm});
            skLineSegment(sketch, "E49.29.0.1", {"start": v(5448.3, 0) * mm, "end": v(5448.3, 1524) * mm});
            skLineSegment(sketch, "E49.29.0.2", {"start": v(5588, 0) * mm, "end": v(5588, 1524) * mm});
            skLineSegment(sketch, "E49.29.0.3", {"start": v(5588, 0) * mm, "end": v(5448.3, 0) * mm});
            skLineSegment(sketch, "E49.30.0.0", {"start": v(5444.5, 1524) * mm, "end": v(5304.8, 1524) * mm});
            skLineSegment(sketch, "E49.30.0.1", {"start": v(5304.8, 0) * mm, "end": v(5304.8, 1524) * mm});
            skLineSegment(sketch, "E49.30.0.2", {"start": v(5444.5, 0) * mm, "end": v(5444.5, 1524) * mm});
            skLineSegment(sketch, "E49.30.0.3", {"start": v(5444.5, 0) * mm, "end": v(5304.8, 0) * mm});
            skLineSegment(sketch, "E49.31.0.0", {"start": v(5300.98, 1524) * mm, "end": v(5161.28, 1524) * mm});
            skLineSegment(sketch, "E49.31.0.1", {"start": v(5161.28, 0) * mm, "end": v(5161.28, 1524) * mm});
            skLineSegment(sketch, "E49.31.0.2", {"start": v(5300.98, 0) * mm, "end": v(5300.98, 1524) * mm});
            skLineSegment(sketch, "E49.31.0.3", {"start": v(5300.98, 0) * mm, "end": v(5161.28, 0) * mm});
            skLineSegment(sketch, "E49.32.0.0", {"start": v(5157.47, 1524) * mm, "end": v(5017.77, 1524) * mm});
            skLineSegment(sketch, "E49.32.0.1", {"start": v(5017.77, 0) * mm, "end": v(5017.77, 1524) * mm});
            skLineSegment(sketch, "E49.32.0.2", {"start": v(5157.47, 0) * mm, "end": v(5157.47, 1524) * mm});
            skLineSegment(sketch, "E49.32.0.3", {"start": v(5157.47, 0) * mm, "end": v(5017.77, 0) * mm});
            skLineSegment(sketch, "E49.33.0.0", {"start": v(5013.96, 1524) * mm, "end": v(4874.26, 1524) * mm});
            skLineSegment(sketch, "E49.33.0.1", {"start": v(4874.26, 0) * mm, "end": v(4874.26, 1524) * mm});
            skLineSegment(sketch, "E49.33.0.2", {"start": v(5013.96, 0) * mm, "end": v(5013.96, 1524) * mm});
            skLineSegment(sketch, "E49.33.0.3", {"start": v(5013.96, 0) * mm, "end": v(4874.26, 0) * mm});
            skLineSegment(sketch, "E49.34.0.0", {"start": v(4870.45, 1524) * mm, "end": v(4730.75, 1524) * mm});
            skLineSegment(sketch, "E49.34.0.1", {"start": v(4730.75, 0) * mm, "end": v(4730.75, 1524) * mm});
            skLineSegment(sketch, "E49.34.0.2", {"start": v(4870.45, 0) * mm, "end": v(4870.45, 1524) * mm});
            skLineSegment(sketch, "E49.34.0.3", {"start": v(4870.45, 0) * mm, "end": v(4730.75, 0) * mm});
            skLineSegment(sketch, "E49.35.0.0", {"start": v(4726.94, 1524) * mm, "end": v(4587.24, 1524) * mm});
            skLineSegment(sketch, "E49.35.0.1", {"start": v(4587.24, 0) * mm, "end": v(4587.24, 1524) * mm});
            skLineSegment(sketch, "E49.35.0.2", {"start": v(4726.94, 0) * mm, "end": v(4726.94, 1524) * mm});
            skLineSegment(sketch, "E49.35.0.3", {"start": v(4726.94, 0) * mm, "end": v(4587.24, 0) * mm});
            skLineSegment(sketch, "E49.36.0.0", {"start": v(4583.43, 1524) * mm, "end": v(4443.73, 1524) * mm});
            skLineSegment(sketch, "E49.36.0.1", {"start": v(4443.73, 0) * mm, "end": v(4443.73, 1524) * mm});
            skLineSegment(sketch, "E49.36.0.2", {"start": v(4583.43, 0) * mm, "end": v(4583.43, 1524) * mm});
            skLineSegment(sketch, "E49.36.0.3", {"start": v(4583.43, 0) * mm, "end": v(4443.73, 0) * mm});
            skLineSegment(sketch, "E49.37.0.0", {"start": v(4439.92, 1524) * mm, "end": v(4300.22, 1524) * mm});
            skLineSegment(sketch, "E49.37.0.1", {"start": v(4300.22, 0) * mm, "end": v(4300.22, 1524) * mm});
            skLineSegment(sketch, "E49.37.0.2", {"start": v(4439.92, 0) * mm, "end": v(4439.92, 1524) * mm});
            skLineSegment(sketch, "E49.37.0.3", {"start": v(4439.92, 0) * mm, "end": v(4300.22, 0) * mm});
            skLineSegment(sketch, "E49.38.0.0", {"start": v(4296.41, 1524) * mm, "end": v(4156.71, 1524) * mm});
            skLineSegment(sketch, "E49.38.0.1", {"start": v(4156.71, 0) * mm, "end": v(4156.71, 1524) * mm});
            skLineSegment(sketch, "E49.38.0.2", {"start": v(4296.41, 0) * mm, "end": v(4296.41, 1524) * mm});
            skLineSegment(sketch, "E49.38.0.3", {"start": v(4296.41, 0) * mm, "end": v(4156.71, 0) * mm});
            skLineSegment(sketch, "E49.39.0.0", {"start": v(4152.9, 1524) * mm, "end": v(4013.2, 1524) * mm});
            skLineSegment(sketch, "E49.39.0.1", {"start": v(4013.2, 0) * mm, "end": v(4013.2, 1524) * mm});
            skLineSegment(sketch, "E49.39.0.2", {"start": v(4152.9, 0) * mm, "end": v(4152.9, 1524) * mm});
            skLineSegment(sketch, "E49.39.0.3", {"start": v(4152.9, 0) * mm, "end": v(4013.2, 0) * mm});
            skLineSegment(sketch, "E49.40.0.0", {"start": v(4009.4, 1524) * mm, "end": v(3869.7, 1524) * mm});
            skLineSegment(sketch, "E49.40.0.1", {"start": v(3869.7, 0) * mm, "end": v(3869.7, 1524) * mm});
            skLineSegment(sketch, "E49.40.0.2", {"start": v(4009.4, 0) * mm, "end": v(4009.4, 1524) * mm});
            skLineSegment(sketch, "E49.40.0.3", {"start": v(4009.4, 0) * mm, "end": v(3869.7, 0) * mm});
            skLineSegment(sketch, "E49.41.0.0", {"start": v(3865.88, 1524) * mm, "end": v(3726.18, 1524) * mm});
            skLineSegment(sketch, "E49.41.0.1", {"start": v(3726.18, 0) * mm, "end": v(3726.18, 1524) * mm});
            skLineSegment(sketch, "E49.41.0.2", {"start": v(3865.88, 0) * mm, "end": v(3865.88, 1524) * mm});
            skLineSegment(sketch, "E49.41.0.3", {"start": v(3865.88, 0) * mm, "end": v(3726.18, 0) * mm});
            skLineSegment(sketch, "E49.42.0.0", {"start": v(3722.37, 1524) * mm, "end": v(3582.67, 1524) * mm});
            skLineSegment(sketch, "E49.42.0.1", {"start": v(3582.67, 0) * mm, "end": v(3582.67, 1524) * mm});
            skLineSegment(sketch, "E49.42.0.2", {"start": v(3722.37, 0) * mm, "end": v(3722.37, 1524) * mm});
            skLineSegment(sketch, "E49.42.0.3", {"start": v(3722.37, 0) * mm, "end": v(3582.67, 0) * mm});
            skLineSegment(sketch, "E49.43.0.0", {"start": v(3578.86, 1524) * mm, "end": v(3439.16, 1524) * mm});
            skLineSegment(sketch, "E49.43.0.1", {"start": v(3439.16, 0) * mm, "end": v(3439.16, 1524) * mm});
            skLineSegment(sketch, "E49.43.0.2", {"start": v(3578.86, 0) * mm, "end": v(3578.86, 1524) * mm});
            skLineSegment(sketch, "E49.43.0.3", {"start": v(3578.86, 0) * mm, "end": v(3439.16, 0) * mm});
            skLineSegment(sketch, "E49.44.0.0", {"start": v(3435.35, 1524) * mm, "end": v(3295.65, 1524) * mm});
            skLineSegment(sketch, "E49.44.0.1", {"start": v(3295.65, 0) * mm, "end": v(3295.65, 1524) * mm});
            skLineSegment(sketch, "E49.44.0.2", {"start": v(3435.35, 0) * mm, "end": v(3435.35, 1524) * mm});
            skLineSegment(sketch, "E49.44.0.3", {"start": v(3435.35, 0) * mm, "end": v(3295.65, 0) * mm});
            skLineSegment(sketch, "E49.45.0.0", {"start": v(3291.84, 1524) * mm, "end": v(3152.14, 1524) * mm});
            skLineSegment(sketch, "E49.45.0.1", {"start": v(3152.14, 0) * mm, "end": v(3152.14, 1524) * mm});
            skLineSegment(sketch, "E49.45.0.2", {"start": v(3291.84, 0) * mm, "end": v(3291.84, 1524) * mm});
            skLineSegment(sketch, "E49.45.0.3", {"start": v(3291.84, 0) * mm, "end": v(3152.14, 0) * mm});
            skLineSegment(sketch, "E49.46.0.0", {"start": v(3148.33, 1524) * mm, "end": v(3008.63, 1524) * mm});
            skLineSegment(sketch, "E49.46.0.1", {"start": v(3008.63, 0) * mm, "end": v(3008.63, 1524) * mm});
            skLineSegment(sketch, "E49.46.0.2", {"start": v(3148.33, 0) * mm, "end": v(3148.33, 1524) * mm});
            skLineSegment(sketch, "E49.46.0.3", {"start": v(3148.33, 0) * mm, "end": v(3008.63, 0) * mm});
            skLineSegment(sketch, "E49.47.0.0", {"start": v(3004.82, 1524) * mm, "end": v(2865.12, 1524) * mm});
            skLineSegment(sketch, "E49.47.0.1", {"start": v(2865.12, 0) * mm, "end": v(2865.12, 1524) * mm});
            skLineSegment(sketch, "E49.47.0.2", {"start": v(3004.82, 0) * mm, "end": v(3004.82, 1524) * mm});
            skLineSegment(sketch, "E49.47.0.3", {"start": v(3004.82, 0) * mm, "end": v(2865.12, 0) * mm});
            skLineSegment(sketch, "E49.48.0.0", {"start": v(2861.31, 1524) * mm, "end": v(2721.61, 1524) * mm});
            skLineSegment(sketch, "E49.48.0.1", {"start": v(2721.61, 0) * mm, "end": v(2721.61, 1524) * mm});
            skLineSegment(sketch, "E49.48.0.2", {"start": v(2861.31, 0) * mm, "end": v(2861.31, 1524) * mm});
            skLineSegment(sketch, "E49.48.0.3", {"start": v(2861.31, 0) * mm, "end": v(2721.61, 0) * mm});
            skLineSegment(sketch, "E49.49.0.0", {"start": v(2717.8, 1524) * mm, "end": v(2578.1, 1524) * mm});
            skLineSegment(sketch, "E49.49.0.1", {"start": v(2578.1, 0) * mm, "end": v(2578.1, 1524) * mm});
            skLineSegment(sketch, "E49.49.0.2", {"start": v(2717.8, 0) * mm, "end": v(2717.8, 1524) * mm});
            skLineSegment(sketch, "E49.49.0.3", {"start": v(2717.8, 0) * mm, "end": v(2578.1, 0) * mm});
            skLineSegment(sketch, "E49.50.0.0", {"start": v(2574.3, 1524) * mm, "end": v(2434.6, 1524) * mm});
            skLineSegment(sketch, "E49.50.0.1", {"start": v(2434.6, 0) * mm, "end": v(2434.6, 1524) * mm});
            skLineSegment(sketch, "E49.50.0.2", {"start": v(2574.3, 0) * mm, "end": v(2574.3, 1524) * mm});
            skLineSegment(sketch, "E49.50.0.3", {"start": v(2574.3, 0) * mm, "end": v(2434.6, 0) * mm});
            skLineSegment(sketch, "E49.51.0.0", {"start": v(2430.78, 1524) * mm, "end": v(2291.08, 1524) * mm});
            skLineSegment(sketch, "E49.51.0.1", {"start": v(2291.08, 0) * mm, "end": v(2291.08, 1524) * mm});
            skLineSegment(sketch, "E49.51.0.2", {"start": v(2430.78, 0) * mm, "end": v(2430.78, 1524) * mm});
            skLineSegment(sketch, "E49.51.0.3", {"start": v(2430.78, 0) * mm, "end": v(2291.08, 0) * mm});
            skLineSegment(sketch, "E49.52.0.0", {"start": v(2287.27, 1524) * mm, "end": v(2147.57, 1524) * mm});
            skLineSegment(sketch, "E49.52.0.1", {"start": v(2147.57, 0) * mm, "end": v(2147.57, 1524) * mm});
            skLineSegment(sketch, "E49.52.0.2", {"start": v(2287.27, 0) * mm, "end": v(2287.27, 1524) * mm});
            skLineSegment(sketch, "E49.52.0.3", {"start": v(2287.27, 0) * mm, "end": v(2147.57, 0) * mm});
            skLineSegment(sketch, "E49.53.0.0", {"start": v(2143.76, 1524) * mm, "end": v(2004.06, 1524) * mm});
            skLineSegment(sketch, "E49.53.0.1", {"start": v(2004.06, 0) * mm, "end": v(2004.06, 1524) * mm});
            skLineSegment(sketch, "E49.53.0.2", {"start": v(2143.76, 0) * mm, "end": v(2143.76, 1524) * mm});
            skLineSegment(sketch, "E49.53.0.3", {"start": v(2143.76, 0) * mm, "end": v(2004.06, 0) * mm});
            skLineSegment(sketch, "E49.54.0.0", {"start": v(2000.25, 1524) * mm, "end": v(1860.55, 1524) * mm});
            skLineSegment(sketch, "E49.54.0.1", {"start": v(1860.55, 0) * mm, "end": v(1860.55, 1524) * mm});
            skLineSegment(sketch, "E49.54.0.2", {"start": v(2000.25, 0) * mm, "end": v(2000.25, 1524) * mm});
            skLineSegment(sketch, "E49.54.0.3", {"start": v(2000.25, 0) * mm, "end": v(1860.55, 0) * mm});
            skLineSegment(sketch, "E49.55.0.0", {"start": v(1856.74, 1524) * mm, "end": v(1717.04, 1524) * mm});
            skLineSegment(sketch, "E49.55.0.1", {"start": v(1717.04, 0) * mm, "end": v(1717.04, 1524) * mm});
            skLineSegment(sketch, "E49.55.0.2", {"start": v(1856.74, 0) * mm, "end": v(1856.74, 1524) * mm});
            skLineSegment(sketch, "E49.55.0.3", {"start": v(1856.74, 0) * mm, "end": v(1717.04, 0) * mm});
            skLineSegment(sketch, "E49.56.0.0", {"start": v(1713.23, 1524) * mm, "end": v(1573.53, 1524) * mm});
            skLineSegment(sketch, "E49.56.0.1", {"start": v(1573.53, 0) * mm, "end": v(1573.53, 1524) * mm});
            skLineSegment(sketch, "E49.56.0.2", {"start": v(1713.23, 0) * mm, "end": v(1713.23, 1524) * mm});
            skLineSegment(sketch, "E49.56.0.3", {"start": v(1713.23, 0) * mm, "end": v(1573.53, 0) * mm});
            skLineSegment(sketch, "E49.57.0.0", {"start": v(1569.72, 1524) * mm, "end": v(1430.02, 1524) * mm});
            skLineSegment(sketch, "E49.57.0.1", {"start": v(1430.02, 0) * mm, "end": v(1430.02, 1524) * mm});
            skLineSegment(sketch, "E49.57.0.2", {"start": v(1569.72, 0) * mm, "end": v(1569.72, 1524) * mm});
            skLineSegment(sketch, "E49.57.0.3", {"start": v(1569.72, 0) * mm, "end": v(1430.02, 0) * mm});
            skLineSegment(sketch, "E49.58.0.0", {"start": v(1426.21, 1524) * mm, "end": v(1286.51, 1524) * mm});
            skLineSegment(sketch, "E49.58.0.1", {"start": v(1286.51, 0) * mm, "end": v(1286.51, 1524) * mm});
            skLineSegment(sketch, "E49.58.0.2", {"start": v(1426.21, 0) * mm, "end": v(1426.21, 1524) * mm});
            skLineSegment(sketch, "E49.58.0.3", {"start": v(1426.21, 0) * mm, "end": v(1286.51, 0) * mm});
            skLineSegment(sketch, "E49.59.0.0", {"start": v(1282.7, 1524) * mm, "end": v(1143, 1524) * mm});
            skLineSegment(sketch, "E49.59.0.1", {"start": v(1143, 0) * mm, "end": v(1143, 1524) * mm});
            skLineSegment(sketch, "E49.59.0.2", {"start": v(1282.7, 0) * mm, "end": v(1282.7, 1524) * mm});
            skLineSegment(sketch, "E49.59.0.3", {"start": v(1282.7, 0) * mm, "end": v(1143, 0) * mm});
            skLineSegment(sketch, "E49.60.0.0", {"start": v(1139.2, 1524) * mm, "end": v(999.5, 1524) * mm});
            skLineSegment(sketch, "E49.60.0.1", {"start": v(999.5, 0) * mm, "end": v(999.5, 1524) * mm});
            skLineSegment(sketch, "E49.60.0.2", {"start": v(1139.2, 0) * mm, "end": v(1139.2, 1524) * mm});
            skLineSegment(sketch, "E49.60.0.3", {"start": v(1139.2, 0) * mm, "end": v(999.5, 0) * mm});
            skLineSegment(sketch, "E49.61.0.0", {"start": v(995.68, 1524) * mm, "end": v(855.98, 1524) * mm});
            skLineSegment(sketch, "E49.61.0.1", {"start": v(855.98, 0) * mm, "end": v(855.98, 1524) * mm});
            skLineSegment(sketch, "E49.61.0.2", {"start": v(995.68, 0) * mm, "end": v(995.68, 1524) * mm});
            skLineSegment(sketch, "E49.61.0.3", {"start": v(995.68, 0) * mm, "end": v(855.98, 0) * mm});
            skLineSegment(sketch, "E49.62.0.0", {"start": v(852.17, 1524) * mm, "end": v(712.47, 1524) * mm});
            skLineSegment(sketch, "E49.62.0.1", {"start": v(712.47, 0) * mm, "end": v(712.47, 1524) * mm});
            skLineSegment(sketch, "E49.62.0.2", {"start": v(852.17, 0) * mm, "end": v(852.17, 1524) * mm});
            skLineSegment(sketch, "E49.62.0.3", {"start": v(852.17, 0) * mm, "end": v(712.47, 0) * mm});
            skLineSegment(sketch, "E49.63.0.0", {"start": v(708.66, 1524) * mm, "end": v(568.96, 1524) * mm});
            skLineSegment(sketch, "E49.63.0.1", {"start": v(568.96, 0) * mm, "end": v(568.96, 1524) * mm});
            skLineSegment(sketch, "E49.63.0.2", {"start": v(708.66, 0) * mm, "end": v(708.66, 1524) * mm});
            skLineSegment(sketch, "E49.63.0.3", {"start": v(708.66, 0) * mm, "end": v(568.96, 0) * mm});
            skLineSegment(sketch, "E49.64.0.0", {"start": v(565.15, 1524) * mm, "end": v(425.45, 1524) * mm});
            skLineSegment(sketch, "E49.64.0.1", {"start": v(425.45, 0) * mm, "end": v(425.45, 1524) * mm});
            skLineSegment(sketch, "E49.64.0.2", {"start": v(565.15, 0) * mm, "end": v(565.15, 1524) * mm});
            skLineSegment(sketch, "E49.64.0.3", {"start": v(565.15, 0) * mm, "end": v(425.45, 0) * mm});
            skLineSegment(sketch, "E49.65.0.0", {"start": v(421.64, 1524) * mm, "end": v(281.94, 1524) * mm});
            skLineSegment(sketch, "E49.65.0.1", {"start": v(281.94, 0) * mm, "end": v(281.94, 1524) * mm});
            skLineSegment(sketch, "E49.65.0.2", {"start": v(421.64, 0) * mm, "end": v(421.64, 1524) * mm});
            skLineSegment(sketch, "E49.65.0.3", {"start": v(421.64, 0) * mm, "end": v(281.94, 0) * mm});
            skLineSegment(sketch, "E49.66.0.0", {"start": v(278.13, 1524) * mm, "end": v(138.43, 1524) * mm});
            skLineSegment(sketch, "E49.66.0.1", {"start": v(138.43, 0) * mm, "end": v(138.43, 1524) * mm});
            skLineSegment(sketch, "E49.66.0.2", {"start": v(278.13, 0) * mm, "end": v(278.13, 1524) * mm});
            skLineSegment(sketch, "E49.66.0.3", {"start": v(278.13, 0) * mm, "end": v(138.43, 0) * mm});
            skLineSegment(sketch, "E49.direction1", {"start": v(9610.1, 1524) * mm, "end": v(9466.58, 1524) * mm, "construction": true});
            skLineSegment(sketch, "E50.bottom", {"start": v(0, 0) * mm, "end": v(134.62, 0) * mm});
            skLineSegment(sketch, "E50.top", {"start": v(0, 1524) * mm, "end": v(134.62, 1524) * mm});
            skLineSegment(sketch, "E50.left", {"start": v(0, 0) * mm, "end": v(0, 1524) * mm});
            skLineSegment(sketch, "E50.right", {"start": v(134.62, 0) * mm, "end": v(134.62, 1524) * mm});
            skSolve(sketch);
        }
        {
            var Q0;
            Q0 = qSketchRegion(id + "F2", true);
            extrude(context, id + "F3", {"entities" : qUnion([Q0]), "operationType" : NewBodyOperationType.ADD, "depth" : 25.4 * mm, "offsetDistance" : 25.4 * mm});
        }
    });
